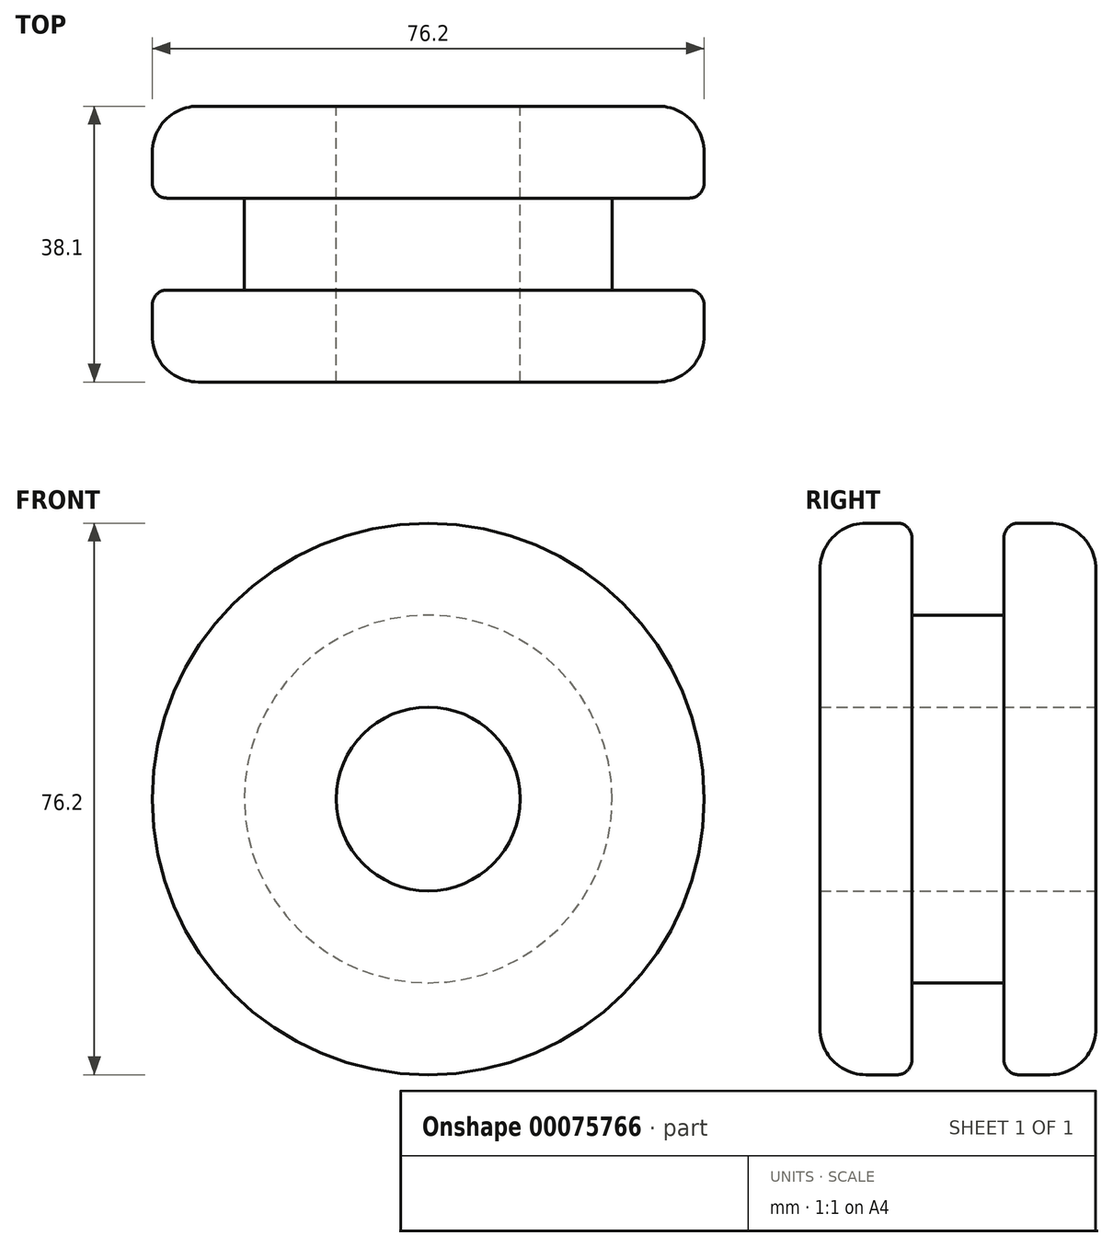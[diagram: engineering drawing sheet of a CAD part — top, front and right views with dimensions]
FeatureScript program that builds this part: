
annotation { "Feature Type Name" : "Feature", "Feature Type Description" : "" }
export const myFeature = defineFeature(function(context is Context, id is Id, definition is map)
    precondition{}
    {
        {
            var Q0;
            Q0=qCreatedBy(makeId("Front.planeOp"),FACE);
            var sketch = newSketch(context, id + "F0", { "sketchPlane" : qUnion([Q0])});
            skCircle(sketch, "E0", {"center": v(0, 0) * mm, "radius": 25.4 * mm});
            skSolve(sketch);
        }
        {
            var Q0;
            Q0=makeQuery(id+"F0.imprint","IMPRINT",FACE,{"disambiguationData":[TD([[makeQuery(id+"F0.imprint","IMPRINT",EDGE,{"derivedFrom":sQuery(id+"F0.wireOp",EDGE,"E0")}),1.0]])]});
            extrude(context, id + "F1", {"entities" : qUnion([Q0]), "endBound" : BoundingType.SYMMETRIC, "depth" : 12.7 * mm});
        }
        {
            var Q0;
            Q0=makeQuery(id+"F1.opExtrude","CAP_FACE",FACE,{"disambiguationData":[OSD([sQuery(id+"F0.wireOp",EDGE,"E0")])],"isStart":false});
            var sketch = newSketch(context, id + "F2", { "sketchPlane" : qUnion([Q0])});
            skCircle(sketch, "E1", {"center": v(0, 0) * mm, "radius": 38.1 * mm});
            skSolve(sketch);
        }
        {
            var Q0;
            Q0=makeQuery(id+"F2.imprint","IMPRINT",FACE,{"disambiguationData":[TD([[makeQuery(id+"F2.imprint","IMPRINT",EDGE,{"derivedFrom":sQuery(id+"F2.wireOp",EDGE,"E1")}),1.0]])]});
            var Q1;
            Q1=makeQuery(id+"F2.imprint","IMPRINT",FACE,{"disambiguationData":[TD([[makeQuery(id+"F2.imprint","IMPRINT",EDGE,{"derivedFrom":makeQuery(id+"F1.opExtrude","CAP_EDGE",EDGE,{"disambiguationData":[OSD([sQuery(id+"F0.wireOp",EDGE,"E0")])],"isStart":false})}),1.0]])]});
            extrude(context, id + "F3", {"entities" : qUnion([Q0, Q1]), "operationType" : NewBodyOperationType.ADD, "depth" : 12.7 * mm});
        }
        {
            var Q0;
            Q0=makeQuery(id+"F1.opExtrude","CAP_FACE",FACE,{"disambiguationData":[OSD([sQuery(id+"F0.wireOp",EDGE,"E0")])],"isStart":true});
            var sketch = newSketch(context, id + "F4", { "sketchPlane" : qUnion([Q0])});
            skCircle(sketch, "E2", {"center": v(0, 0) * mm, "radius": 38.1 * mm});
            skSolve(sketch);
        }
        {
            var Q0;
            Q0=makeQuery(id+"F4.imprint","IMPRINT",FACE,{"disambiguationData":[TD([[makeQuery(id+"F4.imprint","IMPRINT",EDGE,{"derivedFrom":sQuery(id+"F4.wireOp",EDGE,"E2")}),1.0]])]});
            var Q1;
            Q1=makeQuery(id+"F4.imprint","IMPRINT",FACE,{"disambiguationData":[TD([[makeQuery(id+"F4.imprint","IMPRINT",EDGE,{"derivedFrom":makeQuery(id+"F1.opExtrude","CAP_EDGE",EDGE,{"disambiguationData":[OSD([sQuery(id+"F0.wireOp",EDGE,"E0")])],"isStart":true})}),-1.0]])]});
            extrude(context, id + "F5", {"entities" : qUnion([Q0, Q1]), "operationType" : NewBodyOperationType.ADD, "depth" : 12.7 * mm});
        }
        {
            var Q0;
            Q0=makeQuery(id+"F5.opExtrude","CAP_FACE",FACE,{"disambiguationData":[OSD([sQuery(id+"F4.wireOp",EDGE,"E2")])],"isStart":false});
            var sketch = newSketch(context, id + "F6", { "sketchPlane" : qUnion([Q0])});
            skCircle(sketch, "E3", {"center": v(0, 0) * mm, "radius": 12.7 * mm});
            skSolve(sketch);
        }
        {
            var Q0;
            Q0=makeQuery(id+"F6.imprint","IMPRINT",FACE,{"disambiguationData":[TD([[makeQuery(id+"F6.imprint","IMPRINT",EDGE,{"derivedFrom":sQuery(id+"F6.wireOp",EDGE,"E3")}),1.0]])]});
            extrude(context, id + "F7", {"entities" : qUnion([Q0]), "operationType" : NewBodyOperationType.REMOVE, "oppositeDirection" : true, "depth" : 38.1 * mm});
        }
        {
            var Q0;
            Q0=makeQuery(id+"F5.opExtrude","CAP_EDGE",EDGE,{"disambiguationData":[OSD([sQuery(id+"F4.wireOp",EDGE,"E2")])],"isStart":false});
            var Q1;
            Q1=makeQuery(id+"F3.opExtrude","CAP_EDGE",EDGE,{"disambiguationData":[OSD([sQuery(id+"F2.wireOp",EDGE,"E1")])],"isStart":false});
            fillet(context, id + "F8", {"entities" : qUnion([Q0, Q1]), "radius" : 6.35 * mm, "tangentPropagation" : true, "allowEdgeOverflow" : false});
        }
        {
            var Q0;
            Q0=makeQuery(id+"F1.opExtrude","CAP_EDGE",EDGE,{"disambiguationData":[OSD([sQuery(id+"F0.wireOp",EDGE,"E0")])],"isStart":true});
            var Q1;
            Q1=makeQuery(id+"F5.opExtrude","CAP_EDGE",EDGE,{"disambiguationData":[OSD([sQuery(id+"F4.wireOp",EDGE,"E2")])],"isStart":true});
            var Q2;
            Q2=makeQuery(id+"F3.opExtrude","CAP_EDGE",EDGE,{"disambiguationData":[OSD([sQuery(id+"F2.wireOp",EDGE,"E1")])],"isStart":true});
            var Q3;
            Q3=makeQuery(id+"F1.opExtrude","CAP_EDGE",EDGE,{"disambiguationData":[OSD([sQuery(id+"F0.wireOp",EDGE,"E0")])],"isStart":false});
            fillet(context, id + "F9", {"entities" : qUnion([Q0, Q1, Q2, Q3]), "radius" : 2.03 * mm, "tangentPropagation" : true, "allowEdgeOverflow" : false});
        }
    });
